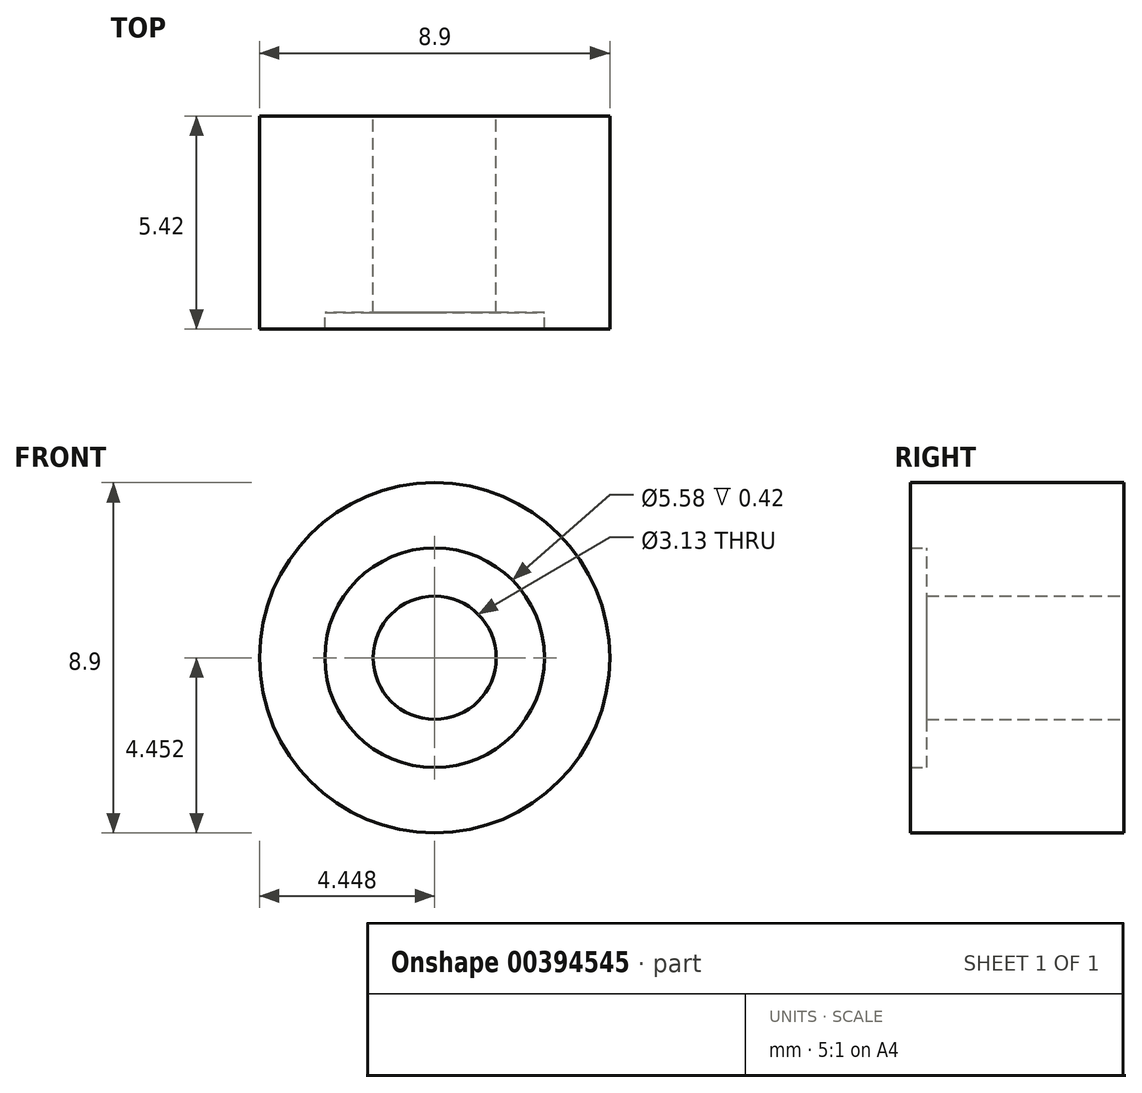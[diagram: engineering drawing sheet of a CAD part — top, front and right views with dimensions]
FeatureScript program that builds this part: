
annotation { "Feature Type Name" : "Feature", "Feature Type Description" : "" }
export const myFeature = defineFeature(function(context is Context, id is Id, definition is map)
    precondition{}
    {
        {
            var Q0;
            Q0=qCreatedBy(makeId("Front.planeOp"),FACE);
            var sketch = newSketch(context, id + "F0", { "sketchPlane" : qUnion([Q0])});
            skCircle(sketch, "E0", {"center": v(-44.58, 35.17) * mm, "radius": 4.45 * mm});
            skCircle(sketch, "E1", {"center": v(-44.58, 35.17) * mm, "radius": 2.8 * mm});
            skCircle(sketch, "E2", {"center": v(-44.58, 35.17) * mm, "radius": 1.56 * mm});
            skSolve(sketch);
        }
        {
            var Q0;
            Q0=makeQuery(id+"F0.imprint","IMPRINT",FACE,{"disambiguationData":[TD([[makeQuery(id+"F0.imprint","IMPRINT",EDGE,{"derivedFrom":sQuery(id+"F0.wireOp",EDGE,"E0")}),1.0]])]});
            extrude(context, id + "F1", {"entities" : qUnion([Q0]), "depth" : 5.42 * mm});
        }
        {
            var Q0;
            Q0=makeQuery(id+"F0.imprint","IMPRINT",FACE,{"disambiguationData":[TD([[makeQuery(id+"F0.imprint","IMPRINT",EDGE,{"derivedFrom":sQuery(id+"F0.wireOp",EDGE,"E1")}),1.0]])]});
            extrude(context, id + "F2", {"entities" : qUnion([Q0]), "operationType" : NewBodyOperationType.ADD, "depth" : 5 * mm});
        }
        {
            var Q0;
            Q0=makeQuery(id+"F0.imprint","IMPRINT",FACE,{"disambiguationData":[TD([[makeQuery(id+"F0.imprint","IMPRINT",EDGE,{"derivedFrom":sQuery(id+"F0.wireOp",EDGE,"E2")}),1.0]])]});
            extrude(context, id + "F3", {"entities" : qUnion([Q0]), "operationType" : NewBodyOperationType.REMOVE, "oppositeDirection" : true, "depth" : 5.42 * mm});
        }
    });
